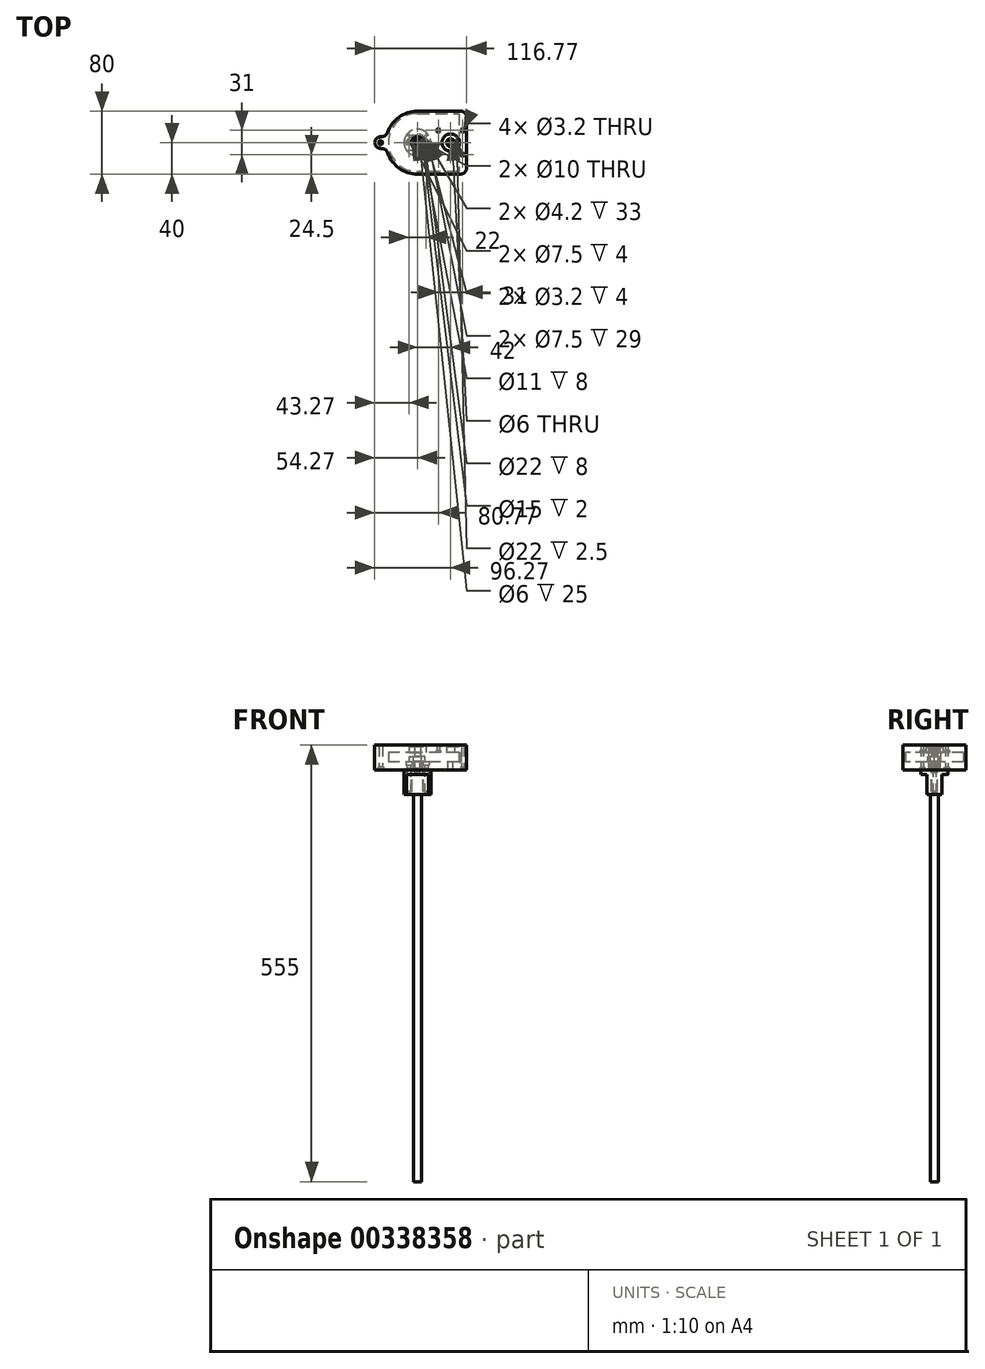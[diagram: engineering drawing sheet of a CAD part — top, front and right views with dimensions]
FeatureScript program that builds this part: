
annotation { "Feature Type Name" : "Feature", "Feature Type Description" : "" }
export const myFeature = defineFeature(function(context is Context, id is Id, definition is map)
    precondition{}
    {
        {
            var Q0;
            Q0=qCreatedBy(makeId("Top.planeOp"),FACE);
            var sketch = newSketch(context, id + "F0", { "sketchPlane" : qUnion([Q0])});
            skCircle(sketch, "E0", {"center": v(0, 0) * mm, "radius": 17 * mm});
            skCircle(sketch, "E1", {"center": v(-11, 0) * mm, "radius": 3.75 * mm});
            skCircle(sketch, "E2", {"center": v(11, 0) * mm, "radius": 3.75 * mm});
            skLineSegment(sketch, "E3", {"start": v(-11, 0) * mm, "end": v(0, 0) * mm, "construction": true});
            skLineSegment(sketch, "E4", {"start": v(0, 0) * mm, "end": v(11, 0) * mm, "construction": true});
            skCircle(sketch, "E5", {"center": v(0, 0) * mm, "radius": 5 * mm});
            skSolve(sketch);
        }
        {
            var Q0;
            Q0=makeQuery(id+"F0.imprint","IMPRINT",FACE,{"disambiguationData":[TD([[makeQuery(id+"F0.imprint","IMPRINT",EDGE,{"derivedFrom":sQuery(id+"F0.wireOp",EDGE,"E0")}),1.0]])]});
            extrude(context, id + "F1", {"entities" : qUnion([Q0]), "oppositeDirection" : true, "depth" : 8 * mm});
        }
        {
            var Q0;
            Q0=makeQuery(id+"F0.imprint","IMPRINT",FACE,{"disambiguationData":[TD([[makeQuery(id+"F0.imprint","IMPRINT",EDGE,{"derivedFrom":sQuery(id+"F0.wireOp",EDGE,"E5")}),1.0]])]});
            extrude(context, id + "F2", {"entities" : qUnion([Q0]), "oppositeDirection" : true, "depth" : 25 * mm});
        }
        {
            var Q0;
            Q0=makeQuery(id+"F2.opExtrude","CAP_FACE",FACE,{"disambiguationData":[OSD([sQuery(id+"F0.wireOp",EDGE,"E5")])],"isStart":true});
            extrude(context, id + "F3", {"entities" : qUnion([Q0]), "operationType" : NewBodyOperationType.ADD, "depth" : 15 * mm});
        }
        {
            var Q0;
            Q0=makeQuery(id+"F3.opExtrude","CAP_FACE",FACE,{"disambiguationData":[OSD([sQuery(id+"F0.wireOp",EDGE,"E5")])],"isStart":false});
            var sketch = newSketch(context, id + "F4", { "sketchPlane" : qUnion([Q0])});
            skCircle(sketch, "E6", {"center": v(0, 0) * mm, "radius": 4 * mm});
            skSolve(sketch);
        }
        {
            var Q0;
            Q0=makeQuery(id+"F4.imprint","IMPRINT",FACE,{"disambiguationData":[TD([[makeQuery(id+"F4.imprint","IMPRINT",EDGE,{"derivedFrom":sQuery(id+"F4.wireOp",EDGE,"E6")}),1.0]])]});
            extrude(context, id + "F5", {"entities" : qUnion([Q0]), "operationType" : NewBodyOperationType.ADD, "depth" : 10 * mm});
        }
        {
            var Q0;
            Q0=makeQuery(id+"F5.opExtrude","CAP_FACE",FACE,{"disambiguationData":[OSD([sQuery(id+"F4.wireOp",EDGE,"E6")])],"isStart":false});
            var sketch = newSketch(context, id + "F6", { "sketchPlane" : qUnion([Q0])});
            skCircle(sketch, "E7", {"center": v(0, 0) * mm, "radius": 3 * mm});
            skSolve(sketch);
        }
        {
            var Q0;
            Q0=makeQuery(id+"F6.imprint","IMPRINT",FACE,{"disambiguationData":[TD([[makeQuery(id+"F6.imprint","IMPRINT",EDGE,{"derivedFrom":sQuery(id+"F6.wireOp",EDGE,"E7")}),1.0]])]});
            extrude(context, id + "F7", {"entities" : qUnion([Q0]), "operationType" : NewBodyOperationType.REMOVE, "oppositeDirection" : true, "depth" : 30 * mm});
        }
        {
            var Q0;
            Q0=makeQuery(id+"F1.opExtrude","CAP_FACE",FACE,{"disambiguationData":[OSD([sQuery(id+"F0.wireOp",EDGE,"E0"),sQuery(id+"F0.wireOp",EDGE,"E1"),sQuery(id+"F0.wireOp",EDGE,"E2"),sQuery(id+"F0.wireOp",EDGE,"E5")])],"isStart":true});
            var sketch = newSketch(context, id + "F8", { "sketchPlane" : qUnion([Q0])});
            skCircle(sketch, "E8.0", {"center": v(0, 0) * mm, "radius": 17 * mm});
            skArc(sketch, "E9", {"start": v(0, 40) * mm, "mid": v(-40, 0) * mm, "end": v(0, -40) * mm});
            skLineSegment(sketch, "E10", {"start": v(0, 40) * mm, "end": v(85, 40) * mm});
            skLineSegment(sketch, "E11", {"start": v(85, 40) * mm, "end": v(85, -40) * mm});
            skLineSegment(sketch, "E12", {"start": v(85, -40) * mm, "end": v(0, -40) * mm});
            skCircle(sketch, "E13", {"center": v(-11, 0) * mm, "radius": 3.5 * mm});
            skCircle(sketch, "E14", {"center": v(11, 0) * mm, "radius": 3.5 * mm});
            skCircle(sketch, "E15", {"center": v(0, 0) * mm, "radius": 5.5 * mm});
            skCircle(sketch, "E16", {"center": v(-11, 0) * mm, "radius": 2.1 * mm});
            skCircle(sketch, "E17", {"center": v(11, 0) * mm, "radius": 2.1 * mm});
            skLineSegment(sketch, "E18", {"start": v(-39.3, 7.5) * mm, "end": v(-54.3, 7.5) * mm});
            skLineSegment(sketch, "E19", {"start": v(-54.3, 7.5) * mm, "end": v(-54.3, -7.5) * mm});
            skLineSegment(sketch, "E20", {"start": v(-54.3, -7.5) * mm, "end": v(-39.3, -7.5) * mm});
            skCircle(sketch, "E21", {"center": v(-46.8, 0) * mm, "radius": 2.1 * mm});
            skLineSegment(sketch, "E22", {"start": v(-46.8, 7.5) * mm, "end": v(-46.8, 0) * mm, "construction": true});
            skSolve(sketch);
        }
        {
            var Q0;
            Q0=makeQuery(id+"F8.imprint","IMPRINT",FACE,{"disambiguationData":[TD([[makeQuery(id+"F8.imprint","IMPRINT",EDGE,{"derivedFrom":sQuery(id+"F8.wireOp",EDGE,"E13")}),1.0]])]});
            var Q1;
            Q1=makeQuery(id+"F8.imprint","IMPRINT",FACE,{"disambiguationData":[TD([[makeQuery(id+"F8.imprint","IMPRINT",EDGE,{"derivedFrom":sQuery(id+"F8.wireOp",EDGE,"E14")}),1.0]])]});
            extrude(context, id + "F9", {"entities" : qUnion([Q0, Q1]), "oppositeDirection" : true, "depth" : 29 * mm});
        }
        {
            var Q0;
            Q0=makeQuery(id+"F8.imprint","IMPRINT",FACE,{"disambiguationData":[TD([[makeQuery(id+"F8.imprint","IMPRINT",EDGE,{"derivedFrom":sQuery(id+"F8.wireOp",EDGE,"E8.0")}),-1.0]])]});
            var Q1;
            Q1=makeQuery(id+"F8.imprint","IMPRINT",FACE,{"disambiguationData":[TD([[makeQuery(id+"F8.imprint","IMPRINT",EDGE,{"derivedFrom":sQuery(id+"F8.wireOp",EDGE,"E8.0")}),1.0]])]});
            var Q2;
            Q2=makeQuery(id+"F8.imprint","IMPRINT",FACE,{"disambiguationData":[TD([[makeQuery(id+"F8.imprint","IMPRINT",EDGE,{"derivedFrom":sQuery(id+"F8.wireOp",EDGE,"E13")}),-1.0]])]});
            var Q3;
            Q3=makeQuery(id+"F8.imprint","IMPRINT",FACE,{"disambiguationData":[TD([[makeQuery(id+"F8.imprint","IMPRINT",EDGE,{"derivedFrom":sQuery(id+"F8.wireOp",EDGE,"E13")}),1.0]])]});
            var Q4;
            Q4=makeQuery(id+"F8.imprint","IMPRINT",FACE,{"disambiguationData":[TD([[makeQuery(id+"F8.imprint","IMPRINT",EDGE,{"derivedFrom":sQuery(id+"F8.wireOp",EDGE,"E14")}),-1.0]])]});
            var Q5;
            Q5=makeQuery(id+"F8.imprint","IMPRINT",FACE,{"disambiguationData":[TD([[makeQuery(id+"F8.imprint","IMPRINT",EDGE,{"derivedFrom":sQuery(id+"F8.wireOp",EDGE,"E14")}),1.0]])]});
            var Q6;
            {var subQ1=sQuery(id+"F8.wireOp",EDGE,"E18");Q6=makeQuery(id+"F8.imprint","IMPRINT",FACE,{"disambiguationData":[TD([[makeQuery(id+"F8.imprint","IMPRINT",EDGE,{"derivedFrom":subQ1}),1.0]])]});}
            extrude(context, id + "F10", {"entities" : qUnion([Q0, Q1, Q2, Q3, Q4, Q5, Q6]), "depth" : 4 * mm});
        }
        {
            var Q0;
            Q0=makeQuery(id+"F10.opExtrude","CAP_FACE",FACE,{"disambiguationData":[OSD([sQuery(id+"F8.wireOp",EDGE,"E9"),sQuery(id+"F8.wireOp",EDGE,"E10"),sQuery(id+"F8.wireOp",EDGE,"E11"),sQuery(id+"F8.wireOp",EDGE,"E12"),sQuery(id+"F8.wireOp",EDGE,"E15"),sQuery(id+"F8.wireOp",EDGE,"E16"),sQuery(id+"F8.wireOp",EDGE,"E17")])],"isStart":false});
            var sketch = newSketch(context, id + "F11", { "sketchPlane" : qUnion([Q0])});
            skCircle(sketch, "E23", {"center": v(-11, 0) * mm, "radius": 3.75 * mm});
            skCircle(sketch, "E24", {"center": v(11, 0) * mm, "radius": 3.75 * mm});
            skSolve(sketch);
        }
        {
            var Q0;
            Q0=makeQuery(id+"F11.imprint","IMPRINT",FACE,{"disambiguationData":[TD([[makeQuery(id+"F11.imprint","IMPRINT",EDGE,{"derivedFrom":sQuery(id+"F11.wireOp",EDGE,"E23")}),-1.0]])]});
            extrude(context, id + "F12", {"entities" : qUnion([Q0]), "operationType" : NewBodyOperationType.ADD, "depth" : 4 * mm});
        }
        {
            var Q0;
            Q0=makeQuery(id+"F3.opExtrude","CAP_FACE",FACE,{"disambiguationData":[OSD([sQuery(id+"F0.wireOp",EDGE,"E5")])],"isStart":false});
            var sketch = newSketch(context, id + "F13", { "sketchPlane" : qUnion([Q0])});
            skCircle(sketch, "E25.cCircle", {"center": v(0, 0) * mm, "radius": 8.5 * mm, "construction": true});
            skLineSegment(sketch, "E25.0", {"start": v(-4.9, 8.5) * mm, "end": v(4.9, 8.5) * mm});
            skLineSegment(sketch, "E25.1", {"start": v(4.9, 8.5) * mm, "end": v(9.81, 0) * mm});
            skLineSegment(sketch, "E25.2", {"start": v(9.81, 0) * mm, "end": v(4.9, -8.5) * mm});
            skLineSegment(sketch, "E25.3", {"start": v(4.9, -8.5) * mm, "end": v(-4.9, -8.5) * mm});
            skLineSegment(sketch, "E25.4", {"start": v(-4.9, -8.5) * mm, "end": v(-9.81, 0) * mm});
            skLineSegment(sketch, "E25.5", {"start": v(-9.81, 0) * mm, "end": v(-4.9, 8.5) * mm});
            skPoint(sketch, "E25.0.midPoint", {"position": v(0, 8.5) * mm});
            skCircle(sketch, "E26.0", {"center": v(0, 0) * mm, "radius": 5 * mm});
            skSolve(sketch);
        }
        {
            var Q0;
            Q0=makeQuery(id+"F13.imprint","IMPRINT",FACE,{"disambiguationData":[TD([[makeQuery(id+"F13.imprint","IMPRINT",EDGE,{"derivedFrom":sQuery(id+"F13.wireOp",EDGE,"E25.0")}),-1.0]])]});
            extrude(context, id + "F14", {"entities" : qUnion([Q0]), "oppositeDirection" : true, "depth" : 6 * mm});
        }
        {
            var Q0;
            Q0=makeQuery(id+"F12.opExtrude","CAP_FACE",FACE,{"disambiguationData":[OSD([sQuery(id+"F8.wireOp",EDGE,"E9"),sQuery(id+"F8.wireOp",EDGE,"E10"),sQuery(id+"F8.wireOp",EDGE,"E11"),sQuery(id+"F8.wireOp",EDGE,"E12"),sQuery(id+"F8.wireOp",EDGE,"E15"),sQuery(id+"F11.wireOp",EDGE,"E23"),sQuery(id+"F11.wireOp",EDGE,"E24")])],"isStart":false});
            var sketch = newSketch(context, id + "F15", { "sketchPlane" : qUnion([Q0])});
            skCircle(sketch, "E27", {"center": v(42, 0) * mm, "radius": 3 * mm});
            skLineSegment(sketch, "E28", {"start": v(57.5, 15.5) * mm, "end": v(57.5, -15.5) * mm, "construction": true});
            skLineSegment(sketch, "E29", {"start": v(57.5, 0) * mm, "end": v(42, 0) * mm, "construction": true});
            skLineSegment(sketch, "E30.bottom", {"start": v(52.5, 40) * mm, "end": v(62.5, 40) * mm});
            skLineSegment(sketch, "E30.top", {"start": v(52.5, -40) * mm, "end": v(62.5, -40) * mm});
            skLineSegment(sketch, "E30.left", {"start": v(52.5, 40) * mm, "end": v(52.5, -40) * mm});
            skLineSegment(sketch, "E30.right", {"start": v(62.5, 40) * mm, "end": v(62.5, -40) * mm});
            skLineSegment(sketch, "E31", {"start": v(57.5, 40) * mm, "end": v(57.5, 15.5) * mm, "construction": true});
            skCircle(sketch, "E32", {"center": v(42, 0) * mm, "radius": 13 * mm});
            skCircle(sketch, "E33", {"center": v(57.5, 15.5) * mm, "radius": 1.6 * mm});
            skCircle(sketch, "E34", {"center": v(57.5, -15.5) * mm, "radius": 1.6 * mm});
            skSolve(sketch);
        }
        {
            var Q0;
            Q0=makeQuery(id+"F15.imprint","IMPRINT",FACE,{"disambiguationData":[TD([[makeQuery(id+"F15.imprint","IMPRINT",EDGE,{"derivedFrom":sQuery(id+"F15.wireOp",EDGE,"E27")}),1.0]])]});
            extrude(context, id + "F16", {"entities" : qUnion([Q0]), "operationType" : NewBodyOperationType.REMOVE, "oppositeDirection" : true, "depth" : 25 * mm});
        }
        {
            var Q0;
            Q0=makeQuery(id+"F15.imprint","IMPRINT",FACE,{"disambiguationData":[TD([[makeQuery(id+"F15.imprint","IMPRINT",EDGE,{"derivedFrom":sQuery(id+"F15.wireOp",EDGE,"E30.bottom")}),-1.0]])]});
            extrude(context, id + "F17", {"entities" : qUnion([Q0]), "operationType" : NewBodyOperationType.ADD, "depth" : 12 * mm});
        }
        {
            var Q0;
            {var subQ0=sQuery(id+"F15.wireOp",EDGE,"E30.right");Q0=makeQuery(id+"F15.imprint","IMPRINT",FACE,{"disambiguationData":[TD([[makeQuery(id+"F15.imprint","IMPRINT",EDGE,{"derivedFrom":subQ0}),1.0]])]});}
            extrude(context, id + "F18", {"entities" : qUnion([Q0]), "operationType" : NewBodyOperationType.REMOVE, "oppositeDirection" : true, "depth" : 25 * mm});
        }
        {
            var Q0;
            {var subQ0=sQuery(id+"F8.wireOp",EDGE,"E15");var subQ1=sQuery(id+"F8.wireOp",EDGE,"E12");var subQ2=sQuery(id+"F8.wireOp",EDGE,"E10");var subQ3=sQuery(id+"F8.wireOp",EDGE,"E9");var subQ4=sQuery(id+"F11.wireOp",EDGE,"E24");var subQ5=sQuery(id+"F11.wireOp",EDGE,"E23");Q0=makeQuery(id+"F17.boolean.opBoolean","SPLIT",FACE,{"disambiguationData":[TD([makeQuery(id+"F10.opExtrude","SWEPT_FACE",FACE,{"disambiguationData":[OSD([subQ3])]})])],"derivedFrom":makeQuery(id+"F12.opExtrude","CAP_FACE",FACE,{"disambiguationData":[OSD([subQ3,subQ2,sQuery(id+"F8.wireOp",EDGE,"E11"),subQ1,subQ0,subQ5,subQ4])],"isStart":false})});}
            var sketch = newSketch(context, id + "F19", { "sketchPlane" : qUnion([Q0])});
            skLineSegment(sketch, "E35.0", {"start": v(0, 37) * mm, "end": v(52.5, 37) * mm});
            skArc(sketch, "E35.1", {"start": v(0, 37) * mm, "mid": v(-37, 0) * mm, "end": v(0, -37) * mm});
            skLineSegment(sketch, "E35.2", {"start": v(52.5, -37) * mm, "end": v(0, -37) * mm});
            skSolve(sketch);
        }
        {
            var Q0;
            Q0=makeQuery(id+"F19.imprint","IMPRINT",FACE,{"disambiguationData":[TD([[makeQuery(id+"F19.imprint","IMPRINT",EDGE,{"derivedFrom":sQuery(id+"F19.wireOp",EDGE,"00304b5b-3b9c-4b06-903c-4d935d8e98f6.0")}),1.0]])]});
            var Q1;
            {var subQ18=sQuery(id+"F19.wireOp",EDGE,"E35.0");Q1=makeQuery(id+"F19.imprint","IMPRINT",FACE,{"disambiguationData":[TD([[makeQuery(id+"F19.imprint","IMPRINT",EDGE,{"derivedFrom":subQ18}),1.0]])]});}
            var Q2;
            Q2=makeQuery(id+"F17.opExtrude","CAP_FACE",FACE,{"disambiguationData":[OSD([sQuery(id+"F15.wireOp",EDGE,"E30.bottom"),sQuery(id+"F15.wireOp",EDGE,"E30.top"),sQuery(id+"F15.wireOp",EDGE,"E30.left"),sQuery(id+"F15.wireOp",EDGE,"E30.right"),sQuery(id+"F15.wireOp",EDGE,"E32"),sQuery(id+"F15.wireOp",EDGE,"E33"),sQuery(id+"F15.wireOp",EDGE,"E34")])],"isStart":false});
            extrude(context, id + "F20", {"entities" : qUnion([Q0, Q1]), "operationType" : NewBodyOperationType.ADD, "endBound" : BoundingType.UP_TO_SURFACE, "endBoundEntityFace" : qUnion([Q2]), "depth" : 25 * mm});
        }
        {
            var Q0;
            {var subQ0=sQuery(id+"F15.wireOp",EDGE,"E34");var subQ1=sQuery(id+"F15.wireOp",EDGE,"E33");var subQ2=sQuery(id+"F15.wireOp",EDGE,"E32");var subQ3=sQuery(id+"F15.wireOp",EDGE,"E30.right");var subQ4=sQuery(id+"F15.wireOp",EDGE,"E30.left");var subQ5=sQuery(id+"F15.wireOp",EDGE,"E30.top");var subQ6=sQuery(id+"F15.wireOp",EDGE,"E30.bottom");Q0=makeQuery(id+"F20.boolean.opBoolean","MERGE",FACE,{"derivedFrom":[makeQuery(id+"F17.opExtrude","CAP_FACE",FACE,{"disambiguationData":[OSD([subQ6,subQ5,subQ4,subQ3,subQ2,subQ1,subQ0])],"isStart":false}),makeQuery(id+"F20.opExtrude","CAP_FACE",FACE,{"disambiguationData":[OSD([subQ6,subQ5,subQ4,subQ3,subQ2,subQ1,subQ0])],"isStart":false})]});}
            var sketch = newSketch(context, id + "F21", { "sketchPlane" : qUnion([Q0])});
            skCircle(sketch, "E36.0", {"center": v(57.5, 15.5) * mm, "radius": 1.6 * mm});
            skCircle(sketch, "E37.0", {"center": v(57.5, -15.5) * mm, "radius": 1.6 * mm});
            skLineSegment(sketch, "E38", {"start": v(57.5, -15.5) * mm, "end": v(26.5, -15.5) * mm, "construction": true});
            skLineSegment(sketch, "E39", {"start": v(26.5, -15.5) * mm, "end": v(26.5, 15.5) * mm, "construction": true});
            skLineSegment(sketch, "E40", {"start": v(26.5, 15.5) * mm, "end": v(57.5, 15.5) * mm, "construction": true});
            skCircle(sketch, "E41", {"center": v(26.5, 15.5) * mm, "radius": 1.6 * mm});
            skCircle(sketch, "E42", {"center": v(26.5, -15.5) * mm, "radius": 1.6 * mm});
            skLineSegment(sketch, "E43.0", {"start": v(62.5, 40) * mm, "end": v(62.5, 40) * mm});
            skLineSegment(sketch, "E44.0", {"start": v(62.5, -40) * mm, "end": v(0, -40) * mm});
            skCircle(sketch, "E45", {"center": v(42, 0) * mm, "radius": 11 * mm});
            skArc(sketch, "E46.0", {"start": v(-39.3, -7.5) * mm, "mid": v(-25.5, -30.82) * mm, "end": v(0, -40) * mm});
            skLineSegment(sketch, "E47.0", {"start": v(-39.3, 7.5) * mm, "end": v(-54.3, 7.5) * mm});
            skLineSegment(sketch, "E48.0", {"start": v(-54.3, -7.5) * mm, "end": v(-39.3, -7.5) * mm});
            skLineSegment(sketch, "E49.0", {"start": v(-54.3, 7.5) * mm, "end": v(-54.3, -7.5) * mm});
            skArc(sketch, "E50.0", {"start": v(0, 40) * mm, "mid": v(-25.5, 30.82) * mm, "end": v(-39.3, 7.5) * mm});
            skLineSegment(sketch, "E51.0", {"start": v(0, 40) * mm, "end": v(62.5, 40) * mm});
            skLineSegment(sketch, "E52.0", {"start": v(62.5, 40) * mm, "end": v(62.5, -40) * mm});
            skCircle(sketch, "E53", {"center": v(42, 0) * mm, "radius": 5 * mm});
            skSolve(sketch);
        }
        {
            var Q0;
            Q0=makeQuery(id+"F21.imprint","IMPRINT",FACE,{"disambiguationData":[TD([[makeQuery(id+"F21.imprint","IMPRINT",EDGE,{"derivedFrom":sQuery(id+"F21.wireOp",EDGE,"E36.0")}),-1.0]])]});
            var Q1;
            Q1=makeQuery(id+"F21.imprint","IMPRINT",FACE,{"disambiguationData":[TD([[makeQuery(id+"F21.imprint","IMPRINT",EDGE,{"derivedFrom":sQuery(id+"F21.wireOp",EDGE,"E41")}),-1.0]])]});
            var Q2;
            Q2=makeQuery(id+"F21.imprint","IMPRINT",FACE,{"disambiguationData":[TD([[makeQuery(id+"F21.imprint","IMPRINT",EDGE,{"derivedFrom":sQuery(id+"F21.wireOp",EDGE,"E45")}),1.0]])]});
            extrude(context, id + "F22", {"entities" : qUnion([Q0, Q1, Q2]), "depth" : 10 * mm});
        }
        {
            var Q0;
            Q0=makeQuery(id+"F10.opExtrude","CAP_FACE",FACE,{"disambiguationData":[OSD([sQuery(id+"F8.wireOp",EDGE,"E9"),sQuery(id+"F8.wireOp",EDGE,"E10"),sQuery(id+"F8.wireOp",EDGE,"E11"),sQuery(id+"F8.wireOp",EDGE,"E12"),sQuery(id+"F8.wireOp",EDGE,"E15"),sQuery(id+"F8.wireOp",EDGE,"E16"),sQuery(id+"F8.wireOp",EDGE,"E17")])],"isStart":true});
            var sketch = newSketch(context, id + "F23", { "sketchPlane" : qUnion([Q0])});
            skCircle(sketch, "E54.0", {"center": v(0, 0) * mm, "radius": 17 * mm});
            skSolve(sketch);
        }
        {
            var Q0;
            Q0=makeQuery(id+"F23.imprint","IMPRINT",FACE,{"disambiguationData":[TD([[makeQuery(id+"F23.imprint","IMPRINT",EDGE,{"derivedFrom":sQuery(id+"F23.wireOp",EDGE,"E54.0")}),-1.0]])]});
            extrude(context, id + "F24", {"entities" : qUnion([Q0]), "operationType" : NewBodyOperationType.ADD, "depth" : 2 * mm});
        }
        {
            var Q0;
            Q0=makeQuery(id+"F5.opExtrude","CAP_FACE",FACE,{"disambiguationData":[OSD([sQuery(id+"F4.wireOp",EDGE,"E6")])],"isStart":false});
            var sketch = newSketch(context, id + "F25", { "sketchPlane" : qUnion([Q0])});
            skCircle(sketch, "E55", {"center": v(0, 0) * mm, "radius": 11 * mm});
            skCircle(sketch, "E56.0", {"center": v(0, 0) * mm, "radius": 4 * mm});
            skSolve(sketch);
        }
        {
            var Q0;
            Q0=makeQuery(id+"F25.imprint","IMPRINT",FACE,{"disambiguationData":[TD([[makeQuery(id+"F25.imprint","IMPRINT",EDGE,{"derivedFrom":sQuery(id+"F25.wireOp",EDGE,"E55")}),1.0]])]});
            extrude(context, id + "F26", {"entities" : qUnion([Q0]), "oppositeDirection" : true, "depth" : 4 * mm});
        }
        {
            var Q0;
            Q0=makeQuery(id+"F26.opExtrude","CAP_FACE",FACE,{"disambiguationData":[OSD([sQuery(id+"F25.wireOp",EDGE,"E55"),sQuery(id+"F25.wireOp",EDGE,"E56.0")])],"isStart":true});
            extrude(context, id + "F27", {"entities" : qUnion([Q0]), "operationType" : NewBodyOperationType.ADD, "depth" : 3 * mm});
        }
        {
            var Q0;
            Q0=makeQuery(id+"F22.opExtrude","CAP_FACE",FACE,{"disambiguationData":[OSD([sQuery(id+"F15.wireOp",EDGE,"E30.right"),sQuery(id+"F21.wireOp",EDGE,"E36.0"),sQuery(id+"F21.wireOp",EDGE,"E37.0"),sQuery(id+"F21.wireOp",EDGE,"E41"),sQuery(id+"F21.wireOp",EDGE,"E42"),sQuery(id+"F21.wireOp",EDGE,"E43.0"),sQuery(id+"F21.wireOp",EDGE,"c1ca0d2d-4cea-42fe-8490-f9553e427049.0"),sQuery(id+"F21.wireOp",EDGE,"E44.0"),sQuery(id+"F21.wireOp",EDGE,"E45")])],"isStart":true});
            var sketch = newSketch(context, id + "F28", { "sketchPlane" : qUnion([Q0])});
            skCircle(sketch, "E57", {"center": v(0, 0) * mm, "radius": 11 * mm});
            skSolve(sketch);
        }
        {
            var Q0;
            Q0=makeQuery(id+"F28.imprint","IMPRINT",FACE,{"disambiguationData":[TD([[makeQuery(id+"F28.imprint","IMPRINT",EDGE,{"derivedFrom":sQuery(id+"F28.wireOp",EDGE,"E57")}),1.0]])]});
            extrude(context, id + "F29", {"entities" : qUnion([Q0]), "operationType" : NewBodyOperationType.REMOVE, "oppositeDirection" : true, "depth" : 8 * mm});
        }
        {
            var Q0;
            Q0=makeQuery(id+"F22.opExtrude","CAP_FACE",FACE,{"disambiguationData":[OSD([sQuery(id+"F8.wireOp",EDGE,"E21"),sQuery(id+"F15.wireOp",EDGE,"E30.bottom"),sQuery(id+"F15.wireOp",EDGE,"E30.top"),sQuery(id+"F15.wireOp",EDGE,"E30.left"),sQuery(id+"F15.wireOp",EDGE,"E30.right"),sQuery(id+"F15.wireOp",EDGE,"E32"),sQuery(id+"F15.wireOp",EDGE,"E33"),sQuery(id+"F15.wireOp",EDGE,"E34"),sQuery(id+"F21.wireOp",EDGE,"E36.0"),sQuery(id+"F21.wireOp",EDGE,"E37.0"),sQuery(id+"F21.wireOp",EDGE,"E41"),sQuery(id+"F21.wireOp",EDGE,"E42"),sQuery(id+"F21.wireOp",EDGE,"E44.0"),sQuery(id+"F21.wireOp",EDGE,"E45"),sQuery(id+"F21.wireOp",EDGE,"E46.0"),sQuery(id+"F21.wireOp",EDGE,"E47.0"),sQuery(id+"F21.wireOp",EDGE,"E48.0"),sQuery(id+"F21.wireOp",EDGE,"E49.0"),sQuery(id+"F21.wireOp",EDGE,"E50.0"),sQuery(id+"F21.wireOp",EDGE,"E51.0"),sQuery(id+"F21.wireOp",EDGE,"E52.0")])],"isStart":true});
            var sketch = newSketch(context, id + "F30", { "sketchPlane" : qUnion([Q0])});
            skCircle(sketch, "E58.cCircle", {"center": v(26.5, 15.5) * mm, "radius": 2.8 * mm, "construction": true});
            skLineSegment(sketch, "E58.0", {"start": v(29.3, 17.12) * mm, "end": v(29.3, 13.88) * mm});
            skLineSegment(sketch, "E58.1", {"start": v(29.3, 13.88) * mm, "end": v(26.5, 12.27) * mm});
            skLineSegment(sketch, "E58.2", {"start": v(26.5, 12.27) * mm, "end": v(23.7, 13.88) * mm});
            skLineSegment(sketch, "E58.3", {"start": v(23.7, 13.88) * mm, "end": v(23.7, 17.12) * mm});
            skLineSegment(sketch, "E58.4", {"start": v(23.7, 17.12) * mm, "end": v(26.5, 18.73) * mm});
            skLineSegment(sketch, "E58.5", {"start": v(26.5, 18.73) * mm, "end": v(29.3, 17.12) * mm});
            skPoint(sketch, "E58.0.midPoint", {"position": v(29.3, 15.5) * mm});
            skCircle(sketch, "E59.cCircle", {"center": v(26.5, -15.5) * mm, "radius": 2.8 * mm, "construction": true});
            skLineSegment(sketch, "E59.0", {"start": v(29.3, -13.88) * mm, "end": v(29.3, -17.12) * mm});
            skLineSegment(sketch, "E59.1", {"start": v(29.3, -17.12) * mm, "end": v(26.5, -18.73) * mm});
            skLineSegment(sketch, "E59.2", {"start": v(26.5, -18.73) * mm, "end": v(23.7, -17.12) * mm});
            skLineSegment(sketch, "E59.3", {"start": v(23.7, -17.12) * mm, "end": v(23.7, -13.88) * mm});
            skLineSegment(sketch, "E59.4", {"start": v(23.7, -13.88) * mm, "end": v(26.5, -12.27) * mm});
            skLineSegment(sketch, "E59.5", {"start": v(26.5, -12.27) * mm, "end": v(29.3, -13.88) * mm});
            skPoint(sketch, "E59.0.midPoint", {"position": v(29.3, -15.5) * mm});
            skSolve(sketch);
        }
        {
            var Q0;
            Q0=makeQuery(id+"F30.imprint","IMPRINT",FACE,{"disambiguationData":[TD([[makeQuery(id+"F30.imprint","IMPRINT",EDGE,{"derivedFrom":sQuery(id+"F30.wireOp",EDGE,"E58.0")}),-1.0]])]});
            var Q1;
            Q1=makeQuery(id+"F30.imprint","IMPRINT",FACE,{"disambiguationData":[TD([[makeQuery(id+"F30.imprint","IMPRINT",EDGE,{"derivedFrom":sQuery(id+"F30.wireOp",EDGE,"E59.0")}),-1.0]])]});
            extrude(context, id + "F31", {"entities" : qUnion([Q0, Q1]), "operationType" : NewBodyOperationType.REMOVE, "oppositeDirection" : true, "depth" : 3 * mm});
        }
        {
            var Q0;
            Q0=makeQuery(id+"F17.boolean.opBoolean","SPLIT",FACE,{"disambiguationData":[TD([makeQuery(id+"F17.opExtrude","SWEPT_FACE",FACE,{"disambiguationData":[OSD([sQuery(id+"F15.wireOp",EDGE,"E33")])]})])],"derivedFrom":makeQuery(id+"F12.opExtrude","CAP_FACE",FACE,{"disambiguationData":[OSD([sQuery(id+"F8.wireOp",EDGE,"E9"),sQuery(id+"F8.wireOp",EDGE,"E10"),sQuery(id+"F8.wireOp",EDGE,"E11"),sQuery(id+"F8.wireOp",EDGE,"E12"),sQuery(id+"F8.wireOp",EDGE,"E15"),sQuery(id+"F8.wireOp",EDGE,"E18"),sQuery(id+"F8.wireOp",EDGE,"E19"),sQuery(id+"F8.wireOp",EDGE,"E20"),sQuery(id+"F8.wireOp",EDGE,"E21"),sQuery(id+"F11.wireOp",EDGE,"E23"),sQuery(id+"F11.wireOp",EDGE,"E24")])],"isStart":false})});
            var Q1;
            Q1=makeQuery(id+"F17.boolean.opBoolean","SPLIT",FACE,{"disambiguationData":[TD([makeQuery(id+"F17.opExtrude","SWEPT_FACE",FACE,{"disambiguationData":[OSD([sQuery(id+"F15.wireOp",EDGE,"E34")])]})])],"derivedFrom":makeQuery(id+"F12.opExtrude","CAP_FACE",FACE,{"disambiguationData":[OSD([sQuery(id+"F8.wireOp",EDGE,"E9"),sQuery(id+"F8.wireOp",EDGE,"E10"),sQuery(id+"F8.wireOp",EDGE,"E11"),sQuery(id+"F8.wireOp",EDGE,"E12"),sQuery(id+"F8.wireOp",EDGE,"E15"),sQuery(id+"F8.wireOp",EDGE,"E18"),sQuery(id+"F8.wireOp",EDGE,"E19"),sQuery(id+"F8.wireOp",EDGE,"E20"),sQuery(id+"F8.wireOp",EDGE,"E21"),sQuery(id+"F11.wireOp",EDGE,"E23"),sQuery(id+"F11.wireOp",EDGE,"E24")])],"isStart":false})});
            extrude(context, id + "F32", {"entities" : qUnion([Q0, Q1]), "operationType" : NewBodyOperationType.REMOVE, "oppositeDirection" : true, "depth" : 25 * mm});
        }
        {
            var Q0;
            Q0=makeQuery(id+"F24.opExtrude","CAP_FACE",FACE,{"disambiguationData":[OSD([sQuery(id+"F8.wireOp",EDGE,"E9"),sQuery(id+"F8.wireOp",EDGE,"E10"),sQuery(id+"F8.wireOp",EDGE,"E11"),sQuery(id+"F8.wireOp",EDGE,"E12"),sQuery(id+"F8.wireOp",EDGE,"E15"),sQuery(id+"F8.wireOp",EDGE,"E16"),sQuery(id+"F8.wireOp",EDGE,"E17"),sQuery(id+"F8.wireOp",EDGE,"E18"),sQuery(id+"F8.wireOp",EDGE,"E19"),sQuery(id+"F8.wireOp",EDGE,"E20"),sQuery(id+"F8.wireOp",EDGE,"E21"),sQuery(id+"F15.wireOp",EDGE,"E27"),sQuery(id+"F15.wireOp",EDGE,"E30.right"),sQuery(id+"F23.wireOp",EDGE,"E54.0")])],"isStart":false});
            var sketch = newSketch(context, id + "F33", { "sketchPlane" : qUnion([Q0])});
            skCircle(sketch, "E60.cCircle", {"center": v(57.5, -15.5) * mm, "radius": 2.8 * mm, "construction": true});
            skLineSegment(sketch, "E60.0", {"start": v(54.7, -17.12) * mm, "end": v(54.7, -13.88) * mm});
            skLineSegment(sketch, "E60.1", {"start": v(54.7, -13.88) * mm, "end": v(57.5, -12.27) * mm});
            skLineSegment(sketch, "E60.2", {"start": v(57.5, -12.27) * mm, "end": v(60.3, -13.88) * mm});
            skLineSegment(sketch, "E60.3", {"start": v(60.3, -13.88) * mm, "end": v(60.3, -17.12) * mm});
            skLineSegment(sketch, "E60.4", {"start": v(60.3, -17.12) * mm, "end": v(57.5, -18.73) * mm});
            skLineSegment(sketch, "E60.5", {"start": v(57.5, -18.73) * mm, "end": v(54.7, -17.12) * mm});
            skPoint(sketch, "E60.0.midPoint", {"position": v(54.7, -15.5) * mm});
            skCircle(sketch, "E61.cCircle", {"center": v(57.5, 15.5) * mm, "radius": 2.8 * mm, "construction": true});
            skLineSegment(sketch, "E61.0", {"start": v(54.7, 13.88) * mm, "end": v(54.7, 17.12) * mm});
            skLineSegment(sketch, "E61.1", {"start": v(54.7, 17.12) * mm, "end": v(57.5, 18.73) * mm});
            skLineSegment(sketch, "E61.2", {"start": v(57.5, 18.73) * mm, "end": v(60.3, 17.12) * mm});
            skLineSegment(sketch, "E61.3", {"start": v(60.3, 17.12) * mm, "end": v(60.3, 13.88) * mm});
            skLineSegment(sketch, "E61.4", {"start": v(60.3, 13.88) * mm, "end": v(57.5, 12.27) * mm});
            skLineSegment(sketch, "E61.5", {"start": v(57.5, 12.27) * mm, "end": v(54.7, 13.88) * mm});
            skPoint(sketch, "E61.0.midPoint", {"position": v(54.7, 15.5) * mm});
            skSolve(sketch);
        }
        {
            var Q0;
            Q0=makeQuery(id+"F33.imprint","IMPRINT",FACE,{"disambiguationData":[TD([[makeQuery(id+"F33.imprint","IMPRINT",EDGE,{"derivedFrom":sQuery(id+"F33.wireOp",EDGE,"E60.0")}),-1.0]])]});
            var Q1;
            Q1=makeQuery(id+"F33.imprint","IMPRINT",FACE,{"disambiguationData":[TD([[makeQuery(id+"F33.imprint","IMPRINT",EDGE,{"derivedFrom":sQuery(id+"F33.wireOp",EDGE,"E61.0")}),-1.0]])]});
            extrude(context, id + "F34", {"entities" : qUnion([Q0, Q1]), "operationType" : NewBodyOperationType.REMOVE, "oppositeDirection" : true, "depth" : 3 * mm});
        }
        {
            var Q0;
            Q0=makeQuery(id+"F24.opExtrude","CAP_FACE",FACE,{"disambiguationData":[OSD([sQuery(id+"F8.wireOp",EDGE,"E9"),sQuery(id+"F8.wireOp",EDGE,"E10"),sQuery(id+"F8.wireOp",EDGE,"E11"),sQuery(id+"F8.wireOp",EDGE,"E12"),sQuery(id+"F8.wireOp",EDGE,"E15"),sQuery(id+"F8.wireOp",EDGE,"E16"),sQuery(id+"F8.wireOp",EDGE,"E17"),sQuery(id+"F8.wireOp",EDGE,"E18"),sQuery(id+"F8.wireOp",EDGE,"E19"),sQuery(id+"F8.wireOp",EDGE,"E20"),sQuery(id+"F8.wireOp",EDGE,"E21"),sQuery(id+"F15.wireOp",EDGE,"E27"),sQuery(id+"F15.wireOp",EDGE,"E30.right"),sQuery(id+"F23.wireOp",EDGE,"E54.0")])],"isStart":false});
            var sketch = newSketch(context, id + "F35", { "sketchPlane" : qUnion([Q0])});
            skCircle(sketch, "E62.cCircle", {"center": v(-46.8, 0) * mm, "radius": 3.5 * mm, "construction": true});
            skLineSegment(sketch, "E62.0", {"start": v(-50.3, -2.02) * mm, "end": v(-50.3, 2.02) * mm});
            skLineSegment(sketch, "E62.1", {"start": v(-50.3, 2.02) * mm, "end": v(-46.8, 4.04) * mm});
            skLineSegment(sketch, "E62.2", {"start": v(-46.8, 4.04) * mm, "end": v(-43.3, 2.02) * mm});
            skLineSegment(sketch, "E62.3", {"start": v(-43.3, 2.02) * mm, "end": v(-43.3, -2.02) * mm});
            skLineSegment(sketch, "E62.4", {"start": v(-43.3, -2.02) * mm, "end": v(-46.8, -4.04) * mm});
            skLineSegment(sketch, "E62.5", {"start": v(-46.8, -4.04) * mm, "end": v(-50.3, -2.02) * mm});
            skPoint(sketch, "E62.0.midPoint", {"position": v(-50.3, 0) * mm});
            skSolve(sketch);
        }
        {
            var Q0;
            Q0=makeQuery(id+"F35.imprint","IMPRINT",FACE,{"disambiguationData":[TD([[makeQuery(id+"F35.imprint","IMPRINT",EDGE,{"derivedFrom":sQuery(id+"F35.wireOp",EDGE,"E62.0")}),-1.0]])]});
            extrude(context, id + "F36", {"entities" : qUnion([Q0]), "operationType" : NewBodyOperationType.REMOVE, "oppositeDirection" : true, "depth" : 4 * mm});
        }
        {
            var Q0;
            {var subQ0=sQuery(id+"F8.wireOp",EDGE,"E12");var subQ1=sQuery(id+"F15.wireOp",EDGE,"E30.right");var subQ2=sQuery(id+"F8.wireOp",EDGE,"E21");var subQ3=sQuery(id+"F8.wireOp",EDGE,"E20");var subQ4=sQuery(id+"F8.wireOp",EDGE,"E19");var subQ5=sQuery(id+"F8.wireOp",EDGE,"E18");var subQ6=sQuery(id+"F8.wireOp",EDGE,"E17");var subQ7=sQuery(id+"F8.wireOp",EDGE,"E16");var subQ8=sQuery(id+"F8.wireOp",EDGE,"E15");var subQ9=sQuery(id+"F8.wireOp",EDGE,"E11");var subQ10=sQuery(id+"F8.wireOp",EDGE,"E10");var subQ11=sQuery(id+"F8.wireOp",EDGE,"E9");var subQ12=sQuery(id+"F15.wireOp",EDGE,"E30.top");Q0=makeQuery(id+"F24.boolean.opBoolean","MERGE",EDGE,{"derivedFrom":[makeQuery(id+"F18.boolean.opBoolean","MERGE",EDGE,{"derivedFrom":[makeQuery(id+"F17.opExtrude","SWEPT_EDGE",EDGE,{"disambiguationData":[OSD([subQ0,subQ12,subQ1])]}),makeQuery(id+"F18.opExtrude","SWEPT_EDGE",EDGE,{"disambiguationData":[OSD([subQ0,subQ12,subQ1])]})]}),makeQuery(id+"F24.opExtrude","SWEPT_EDGE",EDGE,{"disambiguationData":[OSD([subQ11,subQ10,subQ9,subQ0,subQ8,subQ7,subQ6,subQ5,subQ4,subQ3,subQ2,subQ1]),TDD([makeQuery(id+"F23.imprint","INTERSECT",VERTEX,{"derivedFrom":[makeQuery(id+"F18.boolean.opBoolean","INTERSECT",EDGE,{"derivedFrom":[makeQuery(id+"F10.opExtrude","CAP_FACE",FACE,{"disambiguationData":[OSD([subQ11,subQ10,subQ9,subQ0,subQ8,subQ7,subQ6,subQ5,subQ4,subQ3,subQ2])],"isStart":true}),makeQuery(id+"F18.opExtrude","SWEPT_FACE",FACE,{"disambiguationData":[OSD([subQ1])]})]}),makeQuery(id+"F10.opExtrude","CAP_EDGE",EDGE,{"disambiguationData":[OSD([subQ0])],"isStart":true})]})])]})]});}
            var Q1;
            Q1=makeQuery(id+"F22.opExtrude","SWEPT_EDGE",EDGE,{"disambiguationData":[OSD([sQuery(id+"F21.wireOp",EDGE,"E44.0"),sQuery(id+"F21.wireOp",EDGE,"E52.0")])]});
            var Q2;
            {var subQ0=sQuery(id+"F8.wireOp",EDGE,"E10");var subQ1=sQuery(id+"F15.wireOp",EDGE,"E30.right");var subQ2=sQuery(id+"F8.wireOp",EDGE,"E21");var subQ3=sQuery(id+"F8.wireOp",EDGE,"E20");var subQ4=sQuery(id+"F8.wireOp",EDGE,"E19");var subQ5=sQuery(id+"F8.wireOp",EDGE,"E18");var subQ6=sQuery(id+"F8.wireOp",EDGE,"E17");var subQ7=sQuery(id+"F8.wireOp",EDGE,"E16");var subQ8=sQuery(id+"F8.wireOp",EDGE,"E15");var subQ9=sQuery(id+"F8.wireOp",EDGE,"E12");var subQ10=sQuery(id+"F8.wireOp",EDGE,"E11");var subQ11=sQuery(id+"F8.wireOp",EDGE,"E9");var subQ12=sQuery(id+"F15.wireOp",EDGE,"E30.bottom");Q2=makeQuery(id+"F24.boolean.opBoolean","MERGE",EDGE,{"derivedFrom":[makeQuery(id+"F18.boolean.opBoolean","MERGE",EDGE,{"derivedFrom":[makeQuery(id+"F17.opExtrude","SWEPT_EDGE",EDGE,{"disambiguationData":[OSD([subQ0,subQ12,subQ1])]}),makeQuery(id+"F18.opExtrude","SWEPT_EDGE",EDGE,{"disambiguationData":[OSD([subQ0,subQ12,subQ1])]})]}),makeQuery(id+"F24.opExtrude","SWEPT_EDGE",EDGE,{"disambiguationData":[OSD([subQ11,subQ0,subQ10,subQ9,subQ8,subQ7,subQ6,subQ5,subQ4,subQ3,subQ2,subQ1]),TDD([makeQuery(id+"F23.imprint","INTERSECT",VERTEX,{"derivedFrom":[makeQuery(id+"F18.boolean.opBoolean","INTERSECT",EDGE,{"derivedFrom":[makeQuery(id+"F10.opExtrude","CAP_FACE",FACE,{"disambiguationData":[OSD([subQ11,subQ0,subQ10,subQ9,subQ8,subQ7,subQ6,subQ5,subQ4,subQ3,subQ2])],"isStart":true}),makeQuery(id+"F18.opExtrude","SWEPT_FACE",FACE,{"disambiguationData":[OSD([subQ1])]})]}),makeQuery(id+"F10.opExtrude","CAP_EDGE",EDGE,{"disambiguationData":[OSD([subQ0])],"isStart":true})]})])]})]});}
            var Q3;
            Q3=makeQuery(id+"F22.opExtrude","SWEPT_EDGE",EDGE,{"disambiguationData":[OSD([sQuery(id+"F21.wireOp",EDGE,"E51.0"),sQuery(id+"F21.wireOp",EDGE,"E52.0")])]});
            var Q4;
            {var subQ0=sQuery(id+"F8.wireOp",EDGE,"E20");var subQ1=sQuery(id+"F8.wireOp",EDGE,"E9");Q4=makeQuery(id+"F24.boolean.opBoolean","MERGE",EDGE,{"derivedFrom":[makeQuery(id+"F20.boolean.opBoolean","MERGE",EDGE,{"derivedFrom":[makeQuery(id+"F12.boolean.opBoolean","MERGE",EDGE,{"derivedFrom":[makeQuery(id+"F10.opExtrude","SWEPT_EDGE",EDGE,{"disambiguationData":[OSD([subQ1,subQ0])]}),makeQuery(id+"F12.opExtrude","SWEPT_EDGE",EDGE,{"disambiguationData":[OSD([subQ1,subQ0])]})]}),makeQuery(id+"F20.opExtrude","SWEPT_EDGE",EDGE,{"disambiguationData":[OSD([subQ1,subQ0])]})]}),makeQuery(id+"F24.opExtrude","SWEPT_EDGE",EDGE,{"disambiguationData":[OSD([subQ1,subQ0])]})]});}
            var Q5;
            Q5=makeQuery(id+"F22.opExtrude","SWEPT_EDGE",EDGE,{"disambiguationData":[OSD([sQuery(id+"F21.wireOp",EDGE,"E46.0"),sQuery(id+"F21.wireOp",EDGE,"E48.0")])]});
            var Q6;
            Q6=makeQuery(id+"F22.opExtrude","SWEPT_EDGE",EDGE,{"disambiguationData":[OSD([sQuery(id+"F21.wireOp",EDGE,"E48.0"),sQuery(id+"F21.wireOp",EDGE,"E49.0")])]});
            var Q7;
            {var subQ0=sQuery(id+"F8.wireOp",EDGE,"E20");var subQ1=sQuery(id+"F8.wireOp",EDGE,"E19");Q7=makeQuery(id+"F24.boolean.opBoolean","MERGE",EDGE,{"derivedFrom":[makeQuery(id+"F20.boolean.opBoolean","MERGE",EDGE,{"derivedFrom":[makeQuery(id+"F12.boolean.opBoolean","MERGE",EDGE,{"derivedFrom":[makeQuery(id+"F10.opExtrude","SWEPT_EDGE",EDGE,{"disambiguationData":[OSD([subQ1,subQ0])]}),makeQuery(id+"F12.opExtrude","SWEPT_EDGE",EDGE,{"disambiguationData":[OSD([subQ1,subQ0])]})]}),makeQuery(id+"F20.opExtrude","SWEPT_EDGE",EDGE,{"disambiguationData":[OSD([subQ1,subQ0])]})]}),makeQuery(id+"F24.opExtrude","SWEPT_EDGE",EDGE,{"disambiguationData":[OSD([subQ1,subQ0])]})]});}
            var Q8;
            {var subQ0=sQuery(id+"F8.wireOp",EDGE,"E19");var subQ1=sQuery(id+"F8.wireOp",EDGE,"E18");Q8=makeQuery(id+"F24.boolean.opBoolean","MERGE",EDGE,{"derivedFrom":[makeQuery(id+"F20.boolean.opBoolean","MERGE",EDGE,{"derivedFrom":[makeQuery(id+"F12.boolean.opBoolean","MERGE",EDGE,{"derivedFrom":[makeQuery(id+"F10.opExtrude","SWEPT_EDGE",EDGE,{"disambiguationData":[OSD([subQ1,subQ0])]}),makeQuery(id+"F12.opExtrude","SWEPT_EDGE",EDGE,{"disambiguationData":[OSD([subQ1,subQ0])]})]}),makeQuery(id+"F20.opExtrude","SWEPT_EDGE",EDGE,{"disambiguationData":[OSD([subQ1,subQ0])]})]}),makeQuery(id+"F24.opExtrude","SWEPT_EDGE",EDGE,{"disambiguationData":[OSD([subQ1,subQ0])]})]});}
            var Q9;
            Q9=makeQuery(id+"F22.opExtrude","SWEPT_EDGE",EDGE,{"disambiguationData":[OSD([sQuery(id+"F21.wireOp",EDGE,"E47.0"),sQuery(id+"F21.wireOp",EDGE,"E49.0")])]});
            var Q10;
            Q10=makeQuery(id+"F22.opExtrude","SWEPT_EDGE",EDGE,{"disambiguationData":[OSD([sQuery(id+"F21.wireOp",EDGE,"E47.0"),sQuery(id+"F21.wireOp",EDGE,"E50.0")])]});
            var Q11;
            {var subQ0=sQuery(id+"F8.wireOp",EDGE,"E18");var subQ1=sQuery(id+"F8.wireOp",EDGE,"E9");Q11=makeQuery(id+"F24.boolean.opBoolean","MERGE",EDGE,{"derivedFrom":[makeQuery(id+"F20.boolean.opBoolean","MERGE",EDGE,{"derivedFrom":[makeQuery(id+"F12.boolean.opBoolean","MERGE",EDGE,{"derivedFrom":[makeQuery(id+"F10.opExtrude","SWEPT_EDGE",EDGE,{"disambiguationData":[OSD([subQ1,subQ0])]}),makeQuery(id+"F12.opExtrude","SWEPT_EDGE",EDGE,{"disambiguationData":[OSD([subQ1,subQ0])]})]}),makeQuery(id+"F20.opExtrude","SWEPT_EDGE",EDGE,{"disambiguationData":[OSD([subQ1,subQ0])]})]}),makeQuery(id+"F24.opExtrude","SWEPT_EDGE",EDGE,{"disambiguationData":[OSD([subQ1,subQ0])]})]});}
            var Q12;
            Q12=makeQuery(id+"F20.opExtrude","SWEPT_EDGE",EDGE,{"disambiguationData":[OSD([sQuery(id+"F15.wireOp",EDGE,"E30.left"),sQuery(id+"F19.wireOp",EDGE,"E35.0")])]});
            var Q13;
            Q13=makeQuery(id+"F20.opExtrude","SWEPT_EDGE",EDGE,{"disambiguationData":[OSD([sQuery(id+"F15.wireOp",EDGE,"E30.left"),sQuery(id+"F19.wireOp",EDGE,"E35.2")])]});
            fillet(context, id + "F37", {"entities" : qUnion([Q0, Q1, Q2, Q3, Q4, Q5, Q6, Q7, Q8, Q9, Q10, Q11, Q12, Q13]), "radius" : 8 * mm, "tangentPropagation" : true, "allowEdgeOverflow" : false});
        }
        {
            var Q0;
            Q0=makeQuery(id+"F29.boolean.opBoolean","COPY",FACE,{"derivedFrom":makeQuery(id+"F29.opExtrude","CAP_FACE",FACE,{"disambiguationData":[OSD([sQuery(id+"F28.wireOp",EDGE,"E57")])],"isStart":false})});
            var sketch = newSketch(context, id + "F38", { "sketchPlane" : qUnion([Q0])});
            skCircle(sketch, "E63", {"center": v(0, 0) * mm, "radius": 7.5 * mm});
            skSolve(sketch);
        }
        {
            var Q0;
            Q0=makeQuery(id+"F38.imprint","IMPRINT",FACE,{"disambiguationData":[TD([[makeQuery(id+"F38.imprint","IMPRINT",EDGE,{"derivedFrom":sQuery(id+"F38.wireOp",EDGE,"E63")}),1.0]])]});
            extrude(context, id + "F39", {"entities" : qUnion([Q0]), "operationType" : NewBodyOperationType.REMOVE, "oppositeDirection" : true, "depth" : 25 * mm});
        }
        {
            var Q0;
            Q0=makeQuery(id+"F22.opExtrude","CAP_FACE",FACE,{"disambiguationData":[OSD([sQuery(id+"F8.wireOp",EDGE,"E21"),sQuery(id+"F15.wireOp",EDGE,"E30.bottom"),sQuery(id+"F15.wireOp",EDGE,"E30.top"),sQuery(id+"F15.wireOp",EDGE,"E30.left"),sQuery(id+"F15.wireOp",EDGE,"E30.right"),sQuery(id+"F15.wireOp",EDGE,"E32"),sQuery(id+"F15.wireOp",EDGE,"E33"),sQuery(id+"F15.wireOp",EDGE,"E34"),sQuery(id+"F21.wireOp",EDGE,"E36.0"),sQuery(id+"F21.wireOp",EDGE,"E37.0"),sQuery(id+"F21.wireOp",EDGE,"E41"),sQuery(id+"F21.wireOp",EDGE,"E42"),sQuery(id+"F21.wireOp",EDGE,"E44.0"),sQuery(id+"F21.wireOp",EDGE,"E46.0"),sQuery(id+"F21.wireOp",EDGE,"E47.0"),sQuery(id+"F21.wireOp",EDGE,"E48.0"),sQuery(id+"F21.wireOp",EDGE,"E49.0"),sQuery(id+"F21.wireOp",EDGE,"E50.0"),sQuery(id+"F21.wireOp",EDGE,"E51.0"),sQuery(id+"F21.wireOp",EDGE,"E52.0"),sQuery(id+"F21.wireOp",EDGE,"E53")])],"isStart":false});
            var sketch = newSketch(context, id + "F40", { "sketchPlane" : qUnion([Q0])});
            skCircle(sketch, "E64.0", {"center": v(42, 0) * mm, "radius": 11 * mm});
            skSolve(sketch);
        }
        {
            var Q0;
            Q0=makeQuery(id+"F40.imprint","IMPRINT",FACE,{"disambiguationData":[TD([[makeQuery(id+"F40.imprint","IMPRINT",EDGE,{"derivedFrom":sQuery(id+"F40.wireOp",EDGE,"E64.0")}),1.0]])]});
            extrude(context, id + "F41", {"entities" : qUnion([Q0]), "operationType" : NewBodyOperationType.REMOVE, "oppositeDirection" : true, "depth" : 2.5 * mm});
        }
        {
            var Q0;
            Q0=makeQuery(id+"F1.opExtrude","CAP_FACE",FACE,{"disambiguationData":[OSD([sQuery(id+"F0.wireOp",EDGE,"E0"),sQuery(id+"F0.wireOp",EDGE,"E1"),sQuery(id+"F0.wireOp",EDGE,"E2"),sQuery(id+"F0.wireOp",EDGE,"E5")])],"isStart":false});
            var sketch = newSketch(context, id + "F42", { "sketchPlane" : qUnion([Q0])});
            skLineSegment(sketch, "E65", {"start": v(-14.1, 9.5) * mm, "end": v(14.1, 9.5) * mm});
            skLineSegment(sketch, "E66", {"start": v(-14.1, -9.5) * mm, "end": v(14.1, -9.5) * mm});
            skSolve(sketch);
        }
        {
            var Q0;
            {var subQ1=sQuery(id+"F42.wireOp",EDGE,"E65");Q0=makeQuery(id+"F42.imprint","IMPRINT",FACE,{"disambiguationData":[TD([[makeQuery(id+"F42.imprint","IMPRINT",EDGE,{"derivedFrom":subQ1}),-1.0]])]});}
            extrude(context, id + "F43", {"entities" : qUnion([Q0]), "depth" : 25 * mm});
        }
        {
            var Q0;
            Q0=makeQuery(id+"F43.opExtrude","CAP_FACE",FACE,{"disambiguationData":[OSD([sQuery(id+"F0.wireOp",EDGE,"E0"),sQuery(id+"F0.wireOp",EDGE,"E1"),sQuery(id+"F0.wireOp",EDGE,"E2"),sQuery(id+"F0.wireOp",EDGE,"E5"),sQuery(id+"F42.wireOp",EDGE,"E65"),sQuery(id+"F42.wireOp",EDGE,"E66")])],"isStart":false});
            var sketch = newSketch(context, id + "F44", { "sketchPlane" : qUnion([Q0])});
            skCircle(sketch, "E67", {"center": v(-11, 0) * mm, "radius": 1.6 * mm});
            skCircle(sketch, "E68", {"center": v(11, 0) * mm, "radius": 1.6 * mm});
            skSolve(sketch);
        }
        {
            var Q0;
            Q0=makeQuery(id+"F44.imprint","IMPRINT",FACE,{"disambiguationData":[TD([[makeQuery(id+"F44.imprint","IMPRINT",EDGE,{"derivedFrom":sQuery(id+"F44.wireOp",EDGE,"E67")}),-1.0]])]});
            var Q1;
            Q1=makeQuery(id+"F44.imprint","IMPRINT",FACE,{"disambiguationData":[TD([[makeQuery(id+"F44.imprint","IMPRINT",EDGE,{"derivedFrom":sQuery(id+"F44.wireOp",EDGE,"E68")}),-1.0]])]});
            var Q2;
            Q2=makeQuery(id+"F9.opExtrude","CAP_FACE",FACE,{"disambiguationData":[OSD([sQuery(id+"F8.wireOp",EDGE,"E13"),sQuery(id+"F8.wireOp",EDGE,"E16")])],"isStart":false});
            extrude(context, id + "F45", {"entities" : qUnion([Q0, Q1]), "operationType" : NewBodyOperationType.ADD, "endBound" : BoundingType.UP_TO_SURFACE, "oppositeDirection" : true, "endBoundEntityFace" : qUnion([Q2]), "depth" : 25 * mm});
        }
        {
            var Q0;
            Q0=makeQuery(id+"F2.opExtrude","CAP_FACE",FACE,{"disambiguationData":[OSD([sQuery(id+"F0.wireOp",EDGE,"E5")])],"isStart":false});
            extrude(context, id + "F46", {"entities" : qUnion([Q0]), "operationType" : NewBodyOperationType.ADD, "depth" : 500 * mm});
        }
    });
